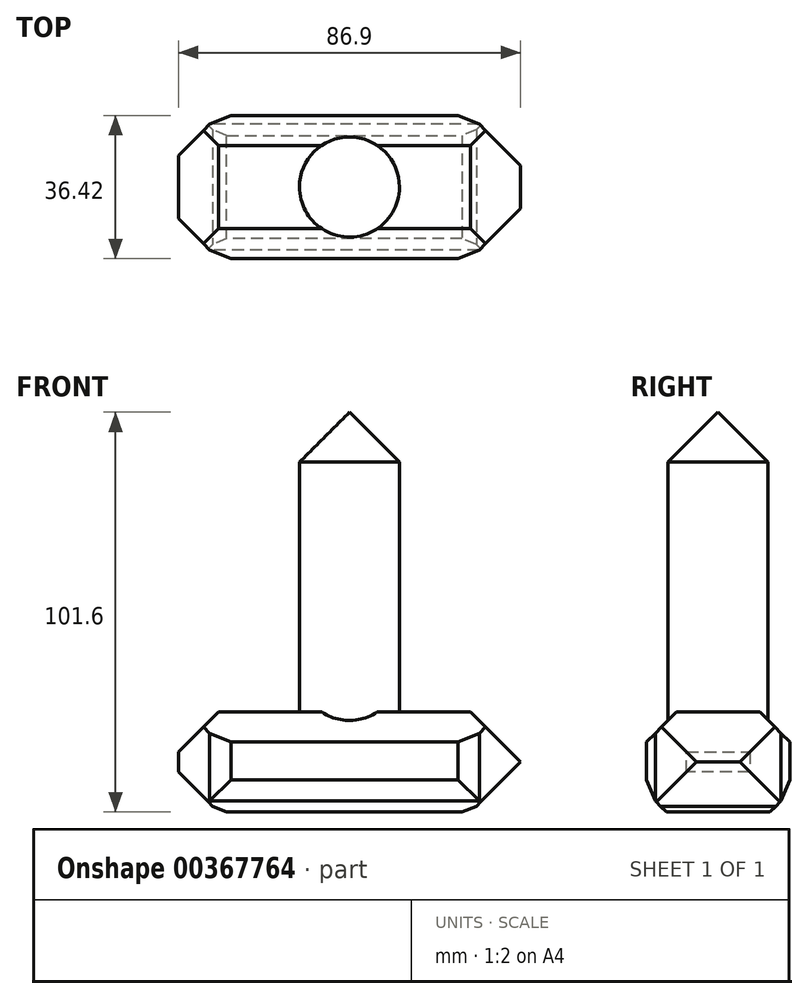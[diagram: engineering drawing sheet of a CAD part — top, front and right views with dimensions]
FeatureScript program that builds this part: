
annotation { "Feature Type Name" : "Feature", "Feature Type Description" : "" }
export const myFeature = defineFeature(function(context is Context, id is Id, definition is map)
    precondition{}
    {
        {
            var Q0;
            Q0=qCreatedBy(makeId("Top.planeOp"),FACE);
            var sketch = newSketch(context, id + "F0", { "sketchPlane" : qUnion([Q0])});
            skCircle(sketch, "E0", {"center": v(0, 0) * mm, "radius": 12.7 * mm});
            skSolve(sketch);
        }
        {
            var Q0;
            Q0 = qSketchRegion(id + "F0", true);
            extrude(context, id + "F1", {"entities" : qUnion([Q0]), "depth" : 101.6 * mm});
        }
        {
            var Q0;
            Q0=qCreatedBy(makeId("Top.planeOp"),FACE);
            var sketch = newSketch(context, id + "F2", { "sketchPlane" : qUnion([Q0])});
            skLineSegment(sketch, "E1.bottom", {"start": v(43.45, -18.21) * mm, "end": v(-43.45, -18.21) * mm});
            skLineSegment(sketch, "E1.top", {"start": v(43.45, 18.21) * mm, "end": v(-43.45, 18.21) * mm});
            skLineSegment(sketch, "E1.left", {"start": v(43.45, -18.21) * mm, "end": v(43.45, 18.21) * mm});
            skLineSegment(sketch, "E1.right", {"start": v(-43.45, -18.21) * mm, "end": v(-43.45, 18.21) * mm});
            skPoint(sketch, "E1.middle", {"position": v(0, 0) * mm});
            skSolve(sketch);
        }
        {
            var Q0;
            Q0 = qSketchRegion(id + "F2", true);
            extrude(context, id + "F3", {"entities" : qUnion([Q0]), "operationType" : NewBodyOperationType.ADD, "depth" : 25.4 * mm});
        }
        {
            var Q0;
            Q0=makeQuery(id+"F3.opExtrude","SWEPT_FACE",FACE,{"disambiguationData":[OSD([sQuery(id+"F2.wireOp",EDGE,"E1.right")])]});
            chamfer(context, id + "F4", {"entities" : qUnion([Q0]), "width" : 10.16 * mm, "tangentPropagation" : true});
        }
        {
            var Q0;
            Q0=makeQuery(id+"F3.opExtrude","SWEPT_FACE",FACE,{"disambiguationData":[OSD([sQuery(id+"F2.wireOp",EDGE,"E1.left")])]});
            chamfer(context, id + "F5", {"entities" : qUnion([Q0]), "width" : 12.7 * mm, "tangentPropagation" : true});
        }
        {
            var Q0;
            Q0=makeQuery(id+"F3.boolean.opBoolean","MERGE",FACE,{"derivedFrom":[makeQuery(id+"F1.opExtrude","CAP_FACE",FACE,{"disambiguationData":[OSD([sQuery(id+"F0.wireOp",EDGE,"E0")])],"isStart":true}),makeQuery(id+"F3.opExtrude","CAP_FACE",FACE,{"disambiguationData":[OSD([sQuery(id+"F2.wireOp",EDGE,"E1.bottom"),sQuery(id+"F2.wireOp",EDGE,"E1.top"),sQuery(id+"F2.wireOp",EDGE,"E1.left"),sQuery(id+"F2.wireOp",EDGE,"E1.right")])],"isStart":true})]});
            chamfer(context, id + "F6", {"entities" : qUnion([Q0]), "width" : 5.08 * mm, "tangentPropagation" : true});
        }
        {
            var Q0;
            Q0=makeQuery(id+"F3.opExtrude","SWEPT_FACE",FACE,{"disambiguationData":[OSD([sQuery(id+"F2.wireOp",EDGE,"E1.bottom")])]});
            chamfer(context, id + "F7", {"entities" : qUnion([Q0]), "width" : 7.62 * mm, "tangentPropagation" : true});
        }
        {
            var Q0;
            Q0=makeQuery(id+"F3.opExtrude","SWEPT_FACE",FACE,{"disambiguationData":[OSD([sQuery(id+"F2.wireOp",EDGE,"E1.top")])]});
            chamfer(context, id + "F8", {"entities" : qUnion([Q0]), "width" : 7.62 * mm, "tangentPropagation" : true});
        }
        {
            var Q0;
            Q0=makeQuery(id+"F1.opExtrude","CAP_FACE",FACE,{"disambiguationData":[OSD([sQuery(id+"F0.wireOp",EDGE,"E0")])],"isStart":false});
            chamfer(context, id + "F9", {"entities" : qUnion([Q0]), "width" : 12.7 * mm, "tangentPropagation" : true});
        }
    });
